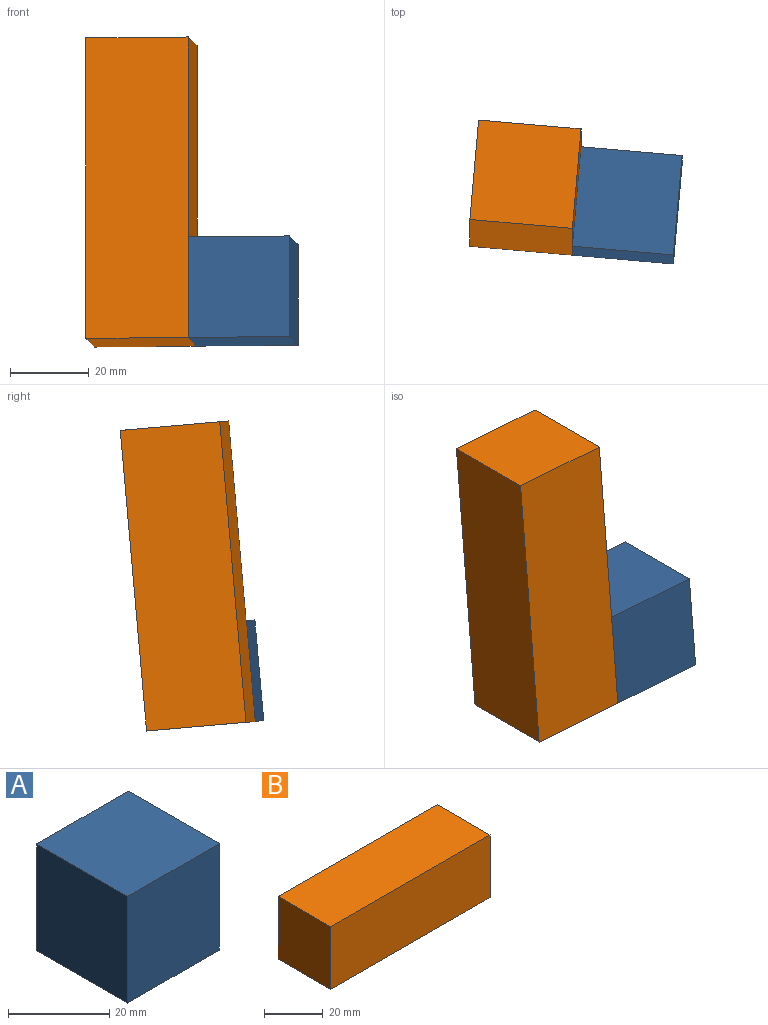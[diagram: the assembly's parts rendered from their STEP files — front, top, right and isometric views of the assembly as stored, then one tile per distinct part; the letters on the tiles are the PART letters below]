
ASSEMBLY  parts=2 mates=1
PART A: 6 faces, bbox 25.6x25.4x25.7 mm
  f0: plane 25.62x25.4mm, normal (0,0,1), area 650.6mm2, adj f1,f3,f4,f5
  f1: plane 25.73x25.4mm, normal (-1,0,0), area 653.7mm2, adj f0,f2,f4,f5
  f2: plane 25.62x25.4mm, normal (0,0,-1), area 650.6mm2, adj f1,f3,f4,f5
  f3: plane 25.73x25.4mm, normal (1,0,0), area 653.7mm2, adj f0,f2,f4,f5
  f4: plane 25.73x25.62mm, normal (0,-1,0), area 659.2mm2, adj f0,f1,f2,f3
  f5: plane 25.73x25.62mm, normal (0,1,0), area 659.2mm2, adj f0,f1,f2,f3
PART B: 6 faces, bbox 76.5x25.4x26.1 mm
  f0: plane 76.5x25.4mm, normal (0,0,1), area 1943.2mm2, adj f1,f3,f4,f5
  f1: plane 26.07x25.4mm, normal (-1,0,0), area 662.2mm2, adj f0,f2,f4,f5
  f2: plane 76.5x25.4mm, normal (0,0,-1), area 1943.2mm2, adj f1,f3,f4,f5
  f3: plane 26.07x25.4mm, normal (1,0,0), area 662.2mm2, adj f0,f2,f4,f5
  f4: plane 76.5x26.07mm, normal (0,-1,0), area 1994.6mm2, adj f0,f1,f2,f3
  f5: plane 76.5x26.07mm, normal (0,1,0), area 1994.6mm2, adj f0,f1,f2,f3
PLACE A rot(axis=(0.71,0,0.71),172.9deg) t=(-46.18,-14.47,81.38)mm
PLACE B rot(axis=(0.71,0,0.71),172.9deg) t=(-43.84,-13.94,89.86)mm
MATE fastened A.f2 <-> B.f0  axis (-1,0.09,-0.01) through (-55.99,-10.47,-28.98)mm
